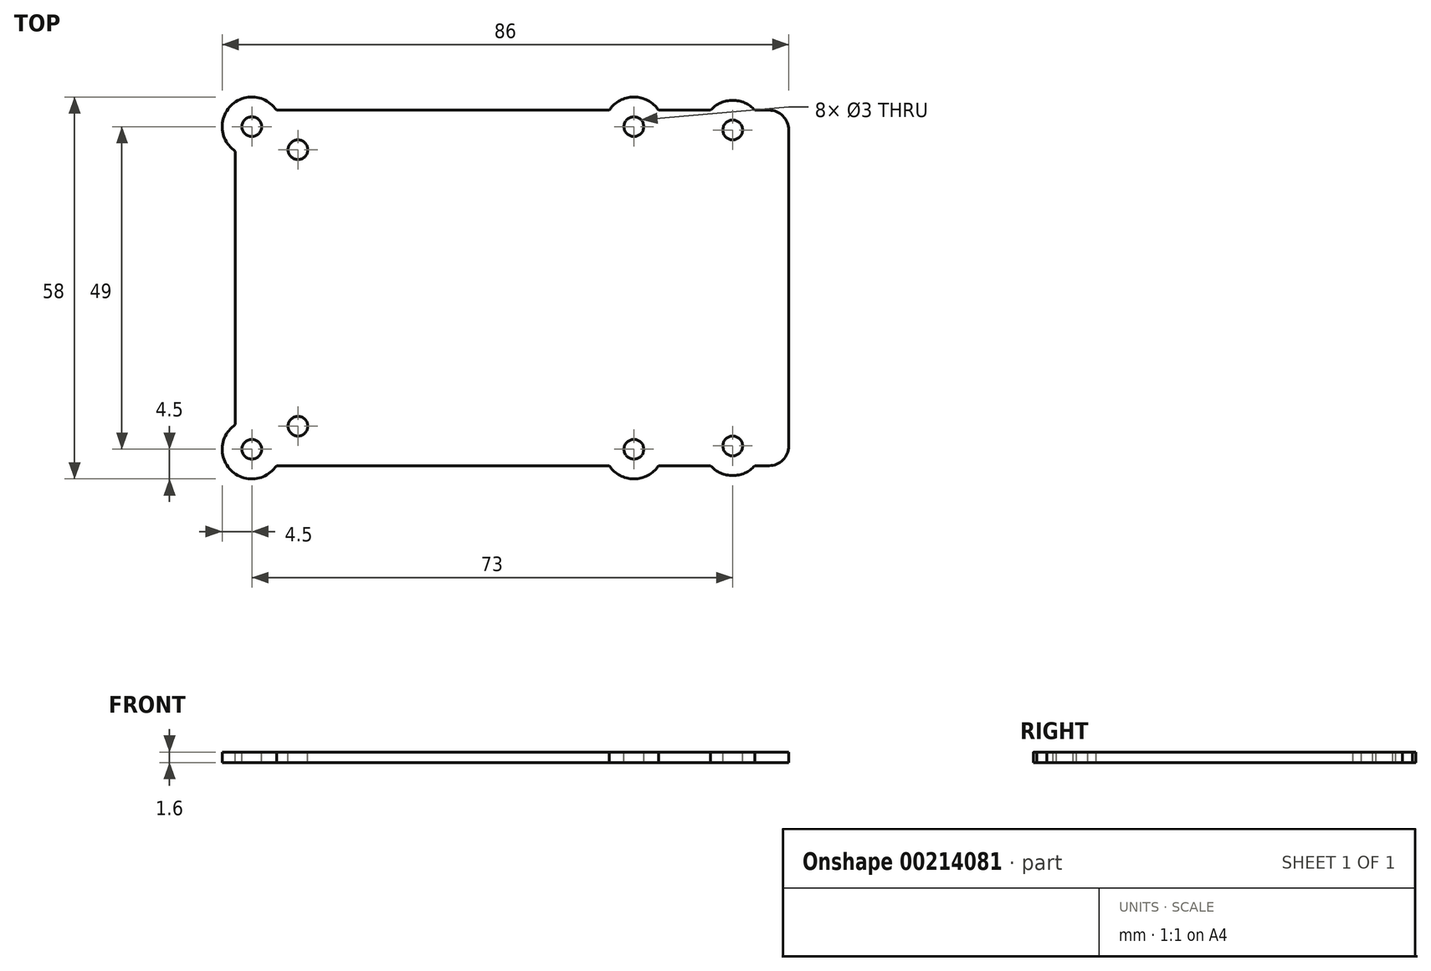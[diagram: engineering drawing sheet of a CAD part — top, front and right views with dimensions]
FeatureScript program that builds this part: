
annotation { "Feature Type Name" : "Feature", "Feature Type Description" : "" }
export const myFeature = defineFeature(function(context is Context, id is Id, definition is map)
    precondition{}
    {
        {
            var Q0;
            Q0=qCreatedBy(makeId("Top.planeOp"),FACE);
            var sketch = newSketch(context, id + "F0", { "sketchPlane" : qUnion([Q0])});
            skLineSegment(sketch, "E0.bottom", {"start": v(39, -27) * mm, "end": v(-39, -27) * mm});
            skLineSegment(sketch, "E0.top", {"start": v(39, 27) * mm, "end": v(-39, 27) * mm});
            skLineSegment(sketch, "E0.left", {"start": v(42, -24) * mm, "end": v(42, 24) * mm});
            skLineSegment(sketch, "E0.right", {"start": v(-42, -24) * mm, "end": v(-42, 24) * mm});
            skPoint(sketch, "E0.middle", {"position": v(0, 0) * mm});
            skPoint(sketch, "E1.visualSharp", {"position": v(-42, 27) * mm});
            skArc(sketch, "E1.filletArc", {"start": v(-39, 27) * mm, "mid": v(-41.12, 26.12) * mm, "end": v(-42, 24) * mm});
            skPoint(sketch, "E2.visualSharp", {"position": v(42, 27) * mm});
            skArc(sketch, "E2.filletArc", {"start": v(42, 24) * mm, "mid": v(41.12, 26.12) * mm, "end": v(39, 27) * mm});
            skPoint(sketch, "E3.visualSharp", {"position": v(42, -27) * mm});
            skArc(sketch, "E3.filletArc", {"start": v(39, -27) * mm, "mid": v(41.12, -26.12) * mm, "end": v(42, -24) * mm});
            skPoint(sketch, "E4.visualSharp", {"position": v(-42, -27) * mm});
            skArc(sketch, "E4.filletArc", {"start": v(-42, -24) * mm, "mid": v(-41.12, -26.12) * mm, "end": v(-39, -27) * mm});
            skSolve(sketch);
        }
        {
            var Q0;
            Q0 = qSketchRegion(id + "F0", true);
            extrude(context, id + "F1", {"entities" : qUnion([Q0]), "depth" : 1.6 * mm});
        }
        {
            var Q0;
            Q0=makeQuery(id+"F1.opExtrude","CAP_FACE",FACE,{"disambiguationData":[OSD([sQuery(id+"F0.wireOp",EDGE,"E0.bottom"),sQuery(id+"F0.wireOp",EDGE,"E0.top"),sQuery(id+"F0.wireOp",EDGE,"E0.left"),sQuery(id+"F0.wireOp",EDGE,"E0.right")])],"isStart":false});
            var sketch = newSketch(context, id + "F2", { "sketchPlane" : qUnion([Q0])});
            skLineSegment(sketch, "E5.bottom", {"start": v(-39.5, 24.5) * mm, "end": v(18.5, 24.5) * mm, "construction": true});
            skLineSegment(sketch, "E5.top", {"start": v(-39.5, -24.5) * mm, "end": v(18.5, -24.5) * mm, "construction": true});
            skLineSegment(sketch, "E5.left", {"start": v(-39.5, 24.5) * mm, "end": v(-39.5, -24.5) * mm, "construction": true});
            skLineSegment(sketch, "E5.right", {"start": v(18.5, 24.5) * mm, "end": v(18.5, -24.5) * mm, "construction": true});
            skCircle(sketch, "E6", {"center": v(-39.5, 24.5) * mm, "radius": 1.5 * mm});
            skCircle(sketch, "E7", {"center": v(18.5, 24.5) * mm, "radius": 1.5 * mm});
            skCircle(sketch, "E8", {"center": v(18.5, -24.5) * mm, "radius": 1.5 * mm});
            skCircle(sketch, "E9", {"center": v(-39.5, -24.5) * mm, "radius": 1.5 * mm});
            skLineSegment(sketch, "E10", {"start": v(-39.5, 0) * mm, "end": v(0, 0) * mm, "construction": true});
            skLineSegment(sketch, "E11", {"start": v(-41.12, 26.12) * mm, "end": v(-39.5, 24.5) * mm});
            skSolve(sketch);
        }
        {
            var Q0;
            Q0 = qSketchRegion(id + "F2", true);
            extrude(context, id + "F3", {"entities" : qUnion([Q0]), "operationType" : NewBodyOperationType.REMOVE, "endBound" : BoundingType.UP_TO_NEXT, "oppositeDirection" : true, "depth" : 2 * mm});
        }
        {
            var Q0;
            Q0=makeQuery(id+"F1.opExtrude","CAP_FACE",FACE,{"disambiguationData":[OSD([sQuery(id+"F0.wireOp",EDGE,"E0.bottom"),sQuery(id+"F0.wireOp",EDGE,"E0.top"),sQuery(id+"F0.wireOp",EDGE,"E0.left"),sQuery(id+"F0.wireOp",EDGE,"E0.right")])],"isStart":false});
            var sketch = newSketch(context, id + "F4", { "sketchPlane" : qUnion([Q0])});
            skLineSegment(sketch, "E12.bottom", {"start": v(-32.5, 24) * mm, "end": v(33.5, 24) * mm, "construction": true});
            skLineSegment(sketch, "E12.top", {"start": v(-32.5, -24) * mm, "end": v(33.5, -24) * mm, "construction": true});
            skLineSegment(sketch, "E12.left", {"start": v(-32.5, 24) * mm, "end": v(-32.5, -24) * mm, "construction": true});
            skLineSegment(sketch, "E12.right", {"start": v(33.5, 24) * mm, "end": v(33.5, -24) * mm, "construction": true});
            skCircle(sketch, "E13", {"center": v(33.5, 24) * mm, "radius": 1.5 * mm});
            skCircle(sketch, "E14", {"center": v(33.5, -24) * mm, "radius": 1.5 * mm});
            skCircle(sketch, "E15", {"center": v(-32.5, 21) * mm, "radius": 1.5 * mm});
            skCircle(sketch, "E16", {"center": v(-32.5, -21) * mm, "radius": 1.5 * mm});
            skLineSegment(sketch, "E17", {"start": v(0, 0) * mm, "end": v(-32.5, 0) * mm, "construction": true});
            skSolve(sketch);
        }
        {
            var Q0;
            Q0 = qSketchRegion(id + "F4", true);
            extrude(context, id + "F5", {"entities" : qUnion([Q0]), "operationType" : NewBodyOperationType.REMOVE, "endBound" : BoundingType.UP_TO_NEXT, "oppositeDirection" : true, "depth" : 25 * mm});
        }
        {
            var Q0;
            Q0=makeQuery(id+"F1.opExtrude","CAP_FACE",FACE,{"disambiguationData":[OSD([sQuery(id+"F0.wireOp",EDGE,"E0.bottom"),sQuery(id+"F0.wireOp",EDGE,"E0.top"),sQuery(id+"F0.wireOp",EDGE,"E0.left"),sQuery(id+"F0.wireOp",EDGE,"E0.right"),sQuery(id+"F0.wireOp",EDGE,"E1.filletArc"),sQuery(id+"F0.wireOp",EDGE,"E2.filletArc"),sQuery(id+"F0.wireOp",EDGE,"E3.filletArc"),sQuery(id+"F0.wireOp",EDGE,"E4.filletArc")])],"isStart":false});
            var sketch = newSketch(context, id + "F6", { "sketchPlane" : qUnion([Q0])});
            skCircle(sketch, "E18", {"center": v(-39.5, 24.5) * mm, "radius": 1.5 * mm});
            skCircle(sketch, "E19", {"center": v(-39.5, 24.5) * mm, "radius": 4.5 * mm});
            skCircle(sketch, "E20", {"center": v(-39.5, -24.5) * mm, "radius": 1.5 * mm});
            skCircle(sketch, "E21", {"center": v(-39.5, -24.5) * mm, "radius": 4.5 * mm});
            skCircle(sketch, "E22", {"center": v(18.5, 24.5) * mm, "radius": 1.5 * mm});
            skCircle(sketch, "E23", {"center": v(18.5, 24.5) * mm, "radius": 4.5 * mm});
            skCircle(sketch, "E24", {"center": v(18.5, -24.5) * mm, "radius": 1.5 * mm});
            skCircle(sketch, "E25", {"center": v(18.5, -24.5) * mm, "radius": 4.5 * mm});
            skCircle(sketch, "E26", {"center": v(33.5, -24) * mm, "radius": 1.5 * mm});
            skCircle(sketch, "E27", {"center": v(33.5, -24) * mm, "radius": 4.5 * mm});
            skCircle(sketch, "E28", {"center": v(33.5, 24) * mm, "radius": 1.5 * mm});
            skCircle(sketch, "E29", {"center": v(33.5, 24) * mm, "radius": 4.5 * mm});
            skSolve(sketch);
        }
        {
            var Q0;
            Q0 = qSketchRegion(id + "F6", true);
            extrude(context, id + "F7", {"entities" : qUnion([Q0]), "operationType" : NewBodyOperationType.ADD, "oppositeDirection" : true, "depth" : 1.6 * mm});
        }
    });
